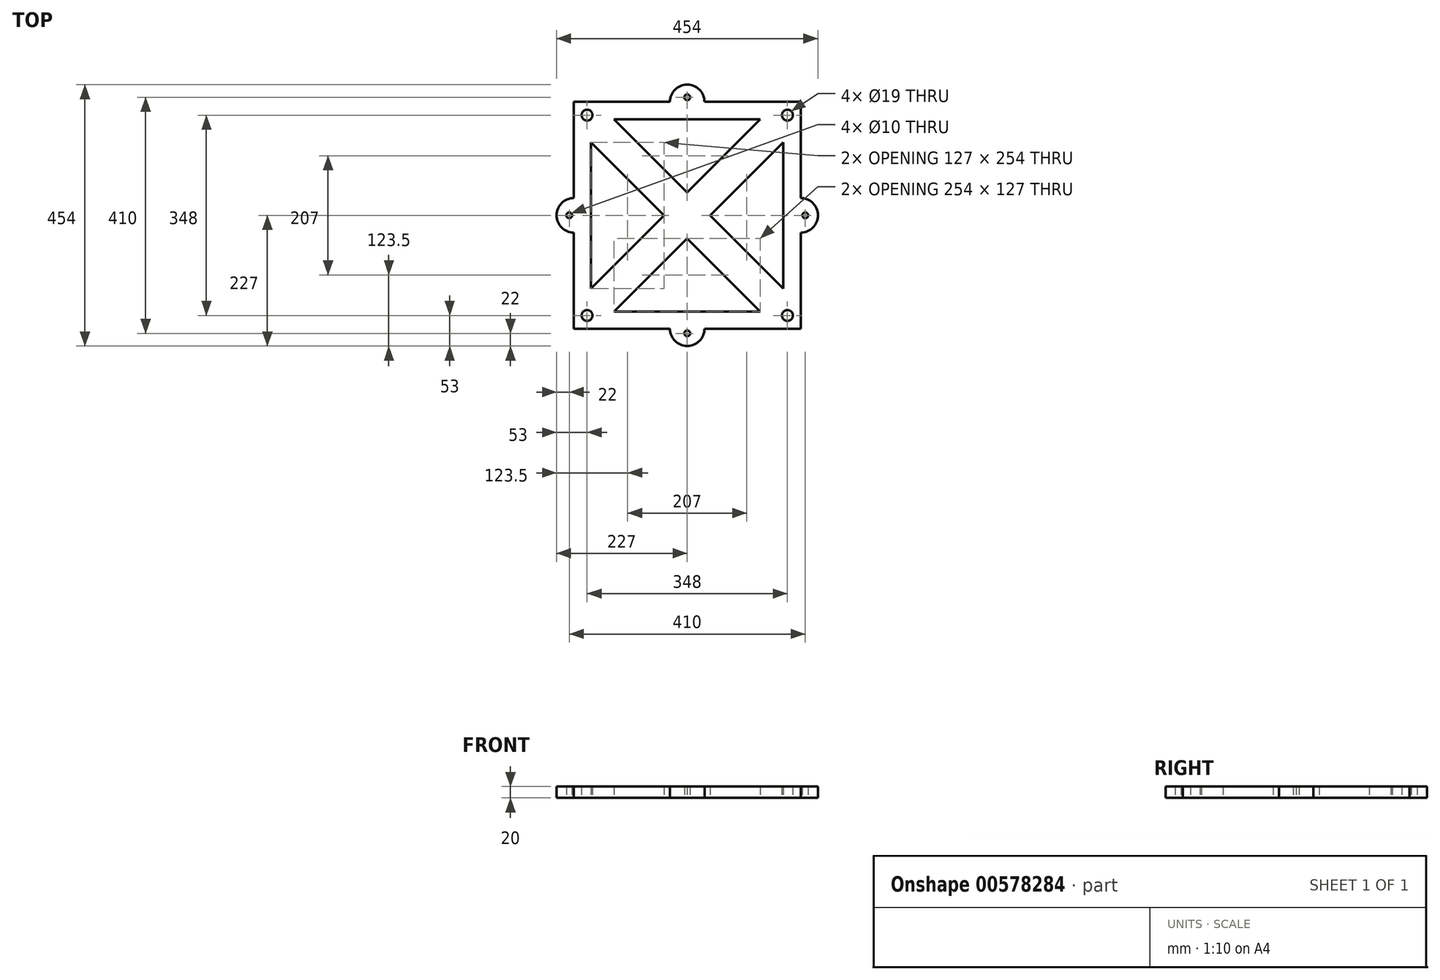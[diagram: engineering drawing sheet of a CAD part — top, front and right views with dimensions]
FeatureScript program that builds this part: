
annotation { "Feature Type Name" : "Feature", "Feature Type Description" : "" }
export const myFeature = defineFeature(function(context is Context, id is Id, definition is map)
    precondition{}
    {
        {
            var Q0;
            Q0=qCreatedBy(makeId("Top.planeOp"),FACE);
            var sketch = newSketch(context, id + "F0", { "sketchPlane" : qUnion([Q0])});
            skLineSegment(sketch, "E0", {"start": v(-167, 127) * mm, "end": v(-127, 167) * mm});
            skLineSegment(sketch, "E1", {"start": v(-127, 167) * mm, "end": v(-127, 197) * mm});
            skLineSegment(sketch, "E2", {"start": v(-127, 197) * mm, "end": v(-197, 197) * mm});
            skLineSegment(sketch, "E3", {"start": v(-197, 197) * mm, "end": v(-197, 127) * mm});
            skLineSegment(sketch, "E4", {"start": v(-197, 127) * mm, "end": v(-167, 127) * mm});
            skCircle(sketch, "E5", {"center": v(-174, 174) * mm, "radius": 9.5 * mm});
            skLineSegment(sketch, "E6.MirrorCS", {"start": v(167, 127) * mm, "end": v(127, 167) * mm});
            skLineSegment(sketch, "E7.MirrorCS", {"start": v(127, 167) * mm, "end": v(127, 197) * mm});
            skLineSegment(sketch, "E8.MirrorCS", {"start": v(127, 197) * mm, "end": v(197, 197) * mm});
            skLineSegment(sketch, "E9.MirrorCS", {"start": v(197, 127) * mm, "end": v(167, 127) * mm});
            skLineSegment(sketch, "E10.MirrorCS", {"start": v(197, 197) * mm, "end": v(197, 127) * mm});
            skCircle(sketch, "E11.MirrorC", {"center": v(174, 174) * mm, "radius": 9.5 * mm});
            skLineSegment(sketch, "E12.MirrorCS", {"start": v(127, -167) * mm, "end": v(127, -197) * mm});
            skLineSegment(sketch, "E13.MirrorCS", {"start": v(127, -197) * mm, "end": v(197, -197) * mm});
            skCircle(sketch, "E14.MirrorC", {"center": v(174, -174) * mm, "radius": 9.5 * mm});
            skLineSegment(sketch, "E15.MirrorCS", {"start": v(167, -127) * mm, "end": v(127, -167) * mm});
            skLineSegment(sketch, "E16.MirrorCS", {"start": v(-127, -197) * mm, "end": v(-197, -197) * mm});
            skLineSegment(sketch, "E17.MirrorCS", {"start": v(-197, -127) * mm, "end": v(-167, -127) * mm});
            skCircle(sketch, "E18.MirrorC", {"center": v(-174, -174) * mm, "radius": 9.5 * mm});
            skLineSegment(sketch, "E19.MirrorCS", {"start": v(-197, -197) * mm, "end": v(-197, -127) * mm});
            skLineSegment(sketch, "E20.MirrorCS", {"start": v(-127, -167) * mm, "end": v(-127, -197) * mm});
            skLineSegment(sketch, "E21.MirrorCS", {"start": v(197, -127) * mm, "end": v(167, -127) * mm});
            skLineSegment(sketch, "E22.MirrorCS", {"start": v(197, -197) * mm, "end": v(197, -127) * mm});
            skLineSegment(sketch, "E23.MirrorCS", {"start": v(-167, -127) * mm, "end": v(-127, -167) * mm});
            skLineSegment(sketch, "E24", {"start": v(-197, 127) * mm, "end": v(-197, -127) * mm});
            skLineSegment(sketch, "E25", {"start": v(-167, 127) * mm, "end": v(-167, -127) * mm});
            skLineSegment(sketch, "E26", {"start": v(-127, 167) * mm, "end": v(127, 167) * mm});
            skLineSegment(sketch, "E27", {"start": v(-127, 197) * mm, "end": v(127, 197) * mm});
            skLineSegment(sketch, "E28", {"start": v(167, 127) * mm, "end": v(167, -127) * mm});
            skLineSegment(sketch, "E29", {"start": v(197, 127) * mm, "end": v(197, -127) * mm});
            skLineSegment(sketch, "E30", {"start": v(127, -167) * mm, "end": v(-127, -167) * mm});
            skLineSegment(sketch, "E31", {"start": v(-127, -197) * mm, "end": v(127, -197) * mm});
            skLineSegment(sketch, "E32", {"start": v(-167, 127) * mm, "end": v(127, -167) * mm});
            skLineSegment(sketch, "E33", {"start": v(-127, 167) * mm, "end": v(167, -127) * mm});
            skLineSegment(sketch, "E34", {"start": v(127, 167) * mm, "end": v(-167, -127) * mm});
            skLineSegment(sketch, "E35", {"start": v(167, 127) * mm, "end": v(-127, -167) * mm});
            skArc(sketch, "E36", {"start": v(-197, 30) * mm, "mid": v(-227, 0) * mm, "end": v(-197, -30) * mm});
            skArc(sketch, "E37.MirrorCS", {"start": v(197, 30) * mm, "mid": v(227, 0) * mm, "end": v(197, -30) * mm});
            skCircle(sketch, "E38", {"center": v(-205, 0) * mm, "radius": 5 * mm});
            skCircle(sketch, "E39.MirrorC", {"center": v(205, 0) * mm, "radius": 5 * mm});
            skArc(sketch, "E40", {"start": v(30, 197) * mm, "mid": v(0, 227) * mm, "end": v(-30, 197) * mm});
            skCircle(sketch, "E41", {"center": v(0, 205) * mm, "radius": 5 * mm});
            skArc(sketch, "E42.MirrorCS", {"start": v(30, -197) * mm, "mid": v(0, -227) * mm, "end": v(-30, -197) * mm});
            skCircle(sketch, "E43.MirrorC", {"center": v(0, -205) * mm, "radius": 5 * mm});
            skSolve(sketch);
        }
        {
            var Q0;
            Q0=qSketchRegion(id+"F0",true);
            var Q1;
            {var subQ0=sQuery(id+"F0.wireOp",EDGE,"E15.MirrorCS");Q1=makeQuery(id+"F0.imprint","IMPRINT",FACE,{"disambiguationData":[TD([[makeQuery(id+"F0.imprint","IMPRINT",EDGE,{"derivedFrom":subQ0}),-1.0]])]});}
            var Q2;
            {var subQ0=sQuery(id+"F0.wireOp",EDGE,"E23.MirrorCS");Q2=makeQuery(id+"F0.imprint","IMPRINT",FACE,{"disambiguationData":[TD([[makeQuery(id+"F0.imprint","IMPRINT",EDGE,{"derivedFrom":subQ0}),1.0]])]});}
            var Q3;
            {var subQ0=sQuery(id+"F0.wireOp",EDGE,"E0");Q3=makeQuery(id+"F0.imprint","IMPRINT",FACE,{"disambiguationData":[TD([[makeQuery(id+"F0.imprint","IMPRINT",EDGE,{"derivedFrom":subQ0}),-1.0]])]});}
            var Q4;
            {var subQ0=sQuery(id+"F0.wireOp",EDGE,"E34");var subQ1=sQuery(id+"F0.wireOp",EDGE,"E32");var subQ2=makeQuery(id+"F0.imprint","INTERSECT",VERTEX,{"derivedFrom":[subQ1,subQ0]});Q4=makeQuery(id+"F0.imprint","IMPRINT",FACE,{"disambiguationData":[TD([[makeQuery(id+"F0.imprint","IMPRINT",EDGE,{"disambiguationData":[TD([[subQ2,-1.0]])],"derivedFrom":subQ1}),1.0]])]});}
            var Q5;
            {var subQ0=sQuery(id+"F0.wireOp",EDGE,"E6.MirrorCS");Q5=makeQuery(id+"F0.imprint","IMPRINT",FACE,{"disambiguationData":[TD([[makeQuery(id+"F0.imprint","IMPRINT",EDGE,{"derivedFrom":subQ0}),1.0]])]});}
            extrude(context, id + "F1", {"entities" : qUnion([Q0, Q1, Q2, Q3, Q4, Q5]), "depth" : 20 * mm, "offsetDistance" : 25 * mm});
        }
    });
